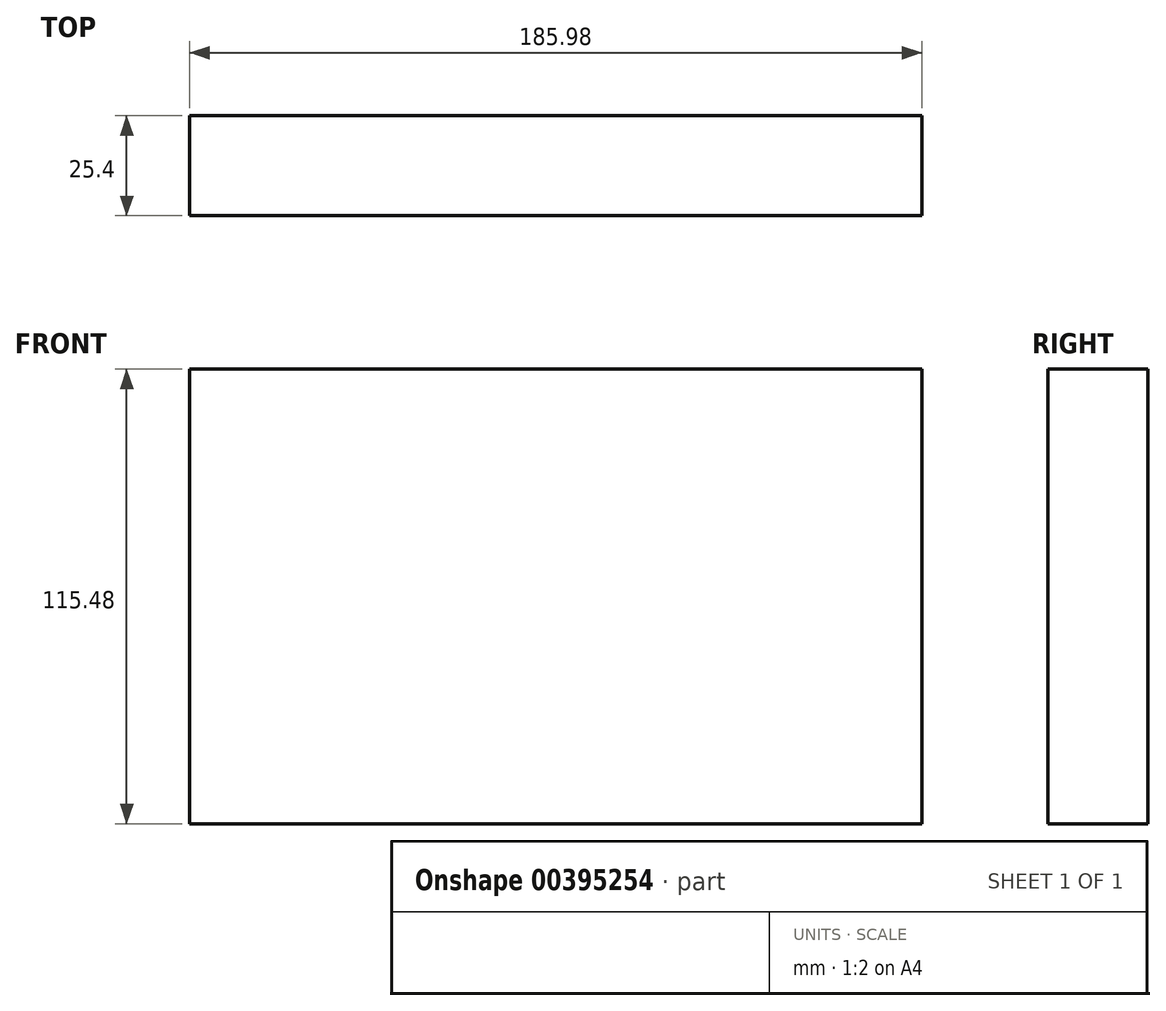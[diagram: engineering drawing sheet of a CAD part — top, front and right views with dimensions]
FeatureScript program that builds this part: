
annotation { "Feature Type Name" : "Feature", "Feature Type Description" : "" }
export const myFeature = defineFeature(function(context is Context, id is Id, definition is map)
    precondition{}
    {
        {
            var Q0;
            Q0=qCreatedBy(makeId("Front.planeOp"),FACE);
            var sketch = newSketch(context, id + "F0", { "sketchPlane" : qUnion([Q0])});
            skLineSegment(sketch, "E0.bottom", {"start": v(-130.58, 49.69) * mm, "end": v(-31.33, 49.69) * mm});
            skLineSegment(sketch, "E0.top", {"start": v(-130.58, -45.32) * mm, "end": v(-31.33, -45.32) * mm});
            skLineSegment(sketch, "E0.left", {"start": v(-130.58, 49.69) * mm, "end": v(-130.58, -45.32) * mm});
            skLineSegment(sketch, "E0.right", {"start": v(-31.33, 49.69) * mm, "end": v(-31.33, -45.32) * mm});
            skSolve(sketch);
        }
        {
            var Q0;
            Q0 = qSketchRegion(id + "F0", true);
            extrude(context, id + "F1", {"entities" : qUnion([Q0]), "depth" : 25.4 * mm});
        }
        {
            var Q0;
            Q0=makeQuery(id+"F1.opExtrude","SWEPT_BODY",BODY,{"disambiguationData":[OSD([sQuery(id+"F0.wireOp",EDGE,"E0.bottom"),sQuery(id+"F0.wireOp",EDGE,"E0.top"),sQuery(id+"F0.wireOp",EDGE,"E0.left"),sQuery(id+"F0.wireOp",EDGE,"E0.right")])]});
            deleteBodies(context, id + "F2", {"entities" : qUnion([Q0])});
        }
        {
            var Q0;
            Q0=qCreatedBy(makeId("Front.planeOp"),FACE);
            var sketch = newSketch(context, id + "F3", { "sketchPlane" : qUnion([Q0])});
            skLineSegment(sketch, "E1.bottom", {"start": v(-137.84, 18.58) * mm, "end": v(48.14, 18.58) * mm});
            skLineSegment(sketch, "E1.top", {"start": v(-137.84, -96.9) * mm, "end": v(48.14, -96.9) * mm});
            skLineSegment(sketch, "E1.left", {"start": v(-137.84, 18.58) * mm, "end": v(-137.84, -96.9) * mm});
            skLineSegment(sketch, "E1.right", {"start": v(48.14, 18.58) * mm, "end": v(48.14, -96.9) * mm});
            skSolve(sketch);
        }
        {
            var Q0;
            Q0 = qSketchRegion(id + "F3", true);
            extrude(context, id + "F4", {"entities" : qUnion([Q0]), "depth" : 25.4 * mm});
        }
    });
